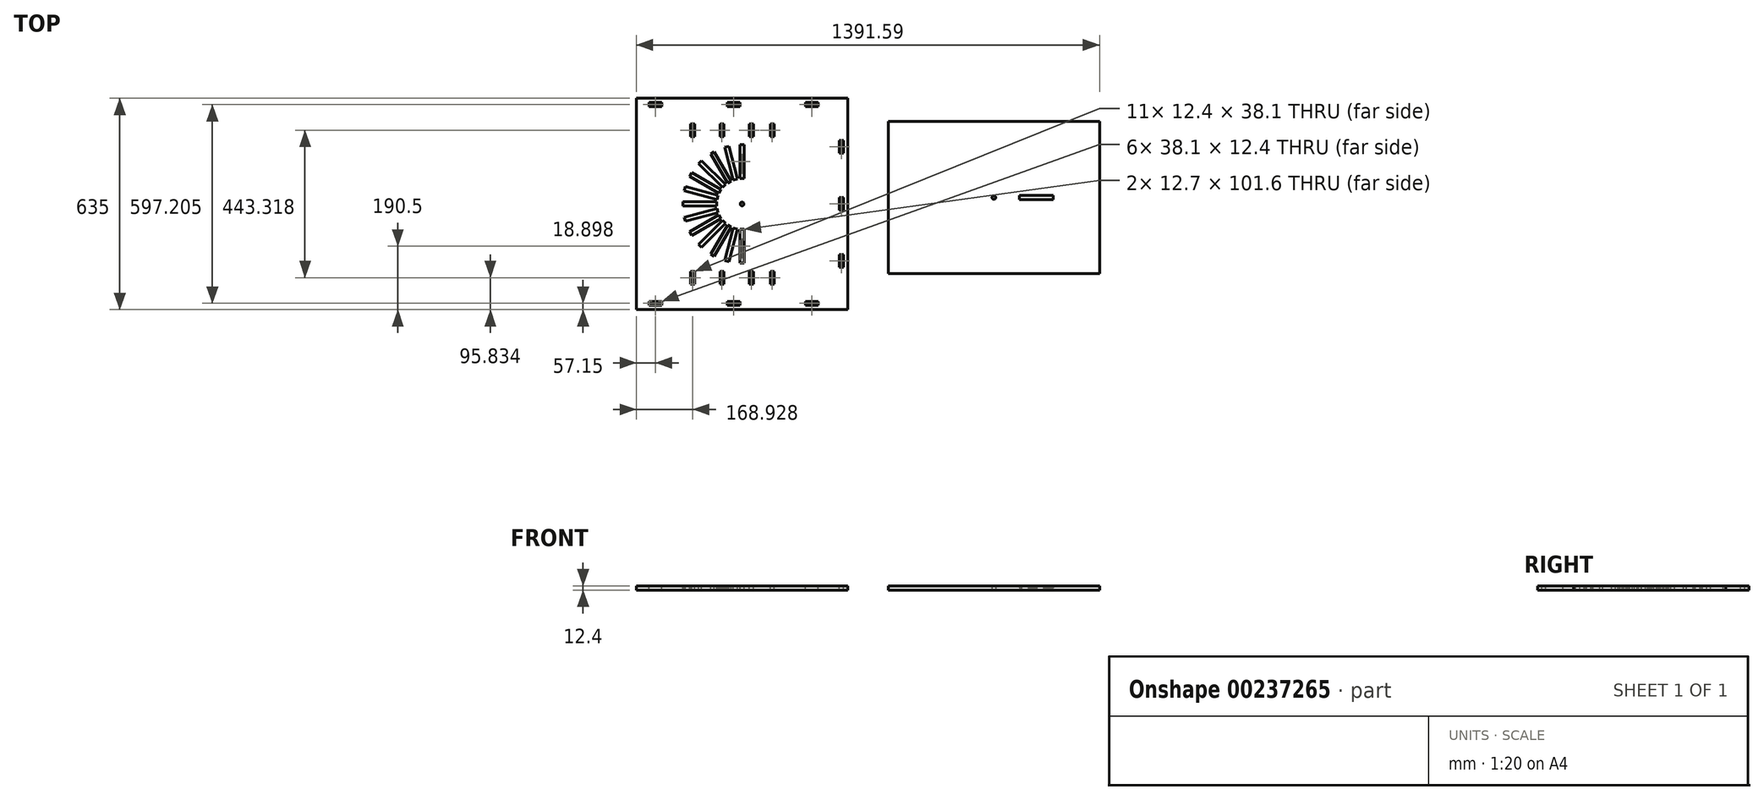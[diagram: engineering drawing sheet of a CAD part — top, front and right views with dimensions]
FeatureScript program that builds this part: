
annotation { "Feature Type Name" : "Feature", "Feature Type Description" : "" }
export const myFeature = defineFeature(function(context is Context, id is Id, definition is map)
    precondition{}
    {
        {
            var Q0;
            Q0=qCreatedBy(makeId("Top.planeOp"),FACE);
            var sketch = newSketch(context, id + "F0", { "sketchPlane" : qUnion([Q0])});
            skLineSegment(sketch, "E0.bottom", {"start": v(0, 0) * mm, "end": v(635, 0) * mm});
            skLineSegment(sketch, "E0.top", {"start": v(0, 635) * mm, "end": v(635, 635) * mm});
            skLineSegment(sketch, "E0.left", {"start": v(0, 0) * mm, "end": v(0, 635) * mm});
            skLineSegment(sketch, "E0.right", {"start": v(635, 0) * mm, "end": v(635, 635) * mm});
            skCircle(sketch, "E1", {"center": v(317.5, 317.5) * mm, "radius": 5.56 * mm});
            skPoint(sketch, "E1.centerSnap0", {"position": v(317.5, 0) * mm});
            skPoint(sketch, "E1.centerSnap1", {"position": v(0, 317.5) * mm});
            skLineSegment(sketch, "E2.bottom", {"start": v(756.6, 108.1) * mm, "end": v(1391.6, 108.1) * mm});
            skLineSegment(sketch, "E2.top", {"start": v(756.6, 565.3) * mm, "end": v(1391.6, 565.3) * mm});
            skLineSegment(sketch, "E2.left", {"start": v(756.6, 108.1) * mm, "end": v(756.6, 565.3) * mm});
            skLineSegment(sketch, "E2.right", {"start": v(1391.6, 108.1) * mm, "end": v(1391.6, 565.3) * mm});
            skCircle(sketch, "E3", {"center": v(1074.1, 336.7) * mm, "radius": 5.56 * mm});
            skPoint(sketch, "E3.centerSnap0", {"position": v(1074.1, 108.1) * mm});
            skPoint(sketch, "E3.centerSnap1", {"position": v(756.6, 336.7) * mm});
            skLineSegment(sketch, "E4.bottom", {"start": v(1251.9, 343.05) * mm, "end": v(1150.3, 343.05) * mm});
            skLineSegment(sketch, "E4.top", {"start": v(1251.9, 330.35) * mm, "end": v(1150.3, 330.35) * mm});
            skLineSegment(sketch, "E4.left", {"start": v(1251.9, 343.05) * mm, "end": v(1251.9, 330.35) * mm});
            skLineSegment(sketch, "E4.right", {"start": v(1150.3, 343.05) * mm, "end": v(1150.3, 330.35) * mm});
            skPoint(sketch, "E4.middle", {"position": v(1201.1, 336.7) * mm});
            skPoint(sketch, "E4.middle.positionSnap0", {"position": v(1391.6, 336.7) * mm});
            skPoint(sketch, "E4.centerSnap0", {"position": v(1391.6, 336.7) * mm});
            skSolve(sketch);
        }
        {
            var Q0;
            Q0 = qSketchRegion(id + "F0", true);
            extrude(context, id + "F1", {"entities" : qUnion([Q0]), "depth" : 12.4 * mm});
        }
        {
            var Q0;
            Q0=makeQuery(id+"F1.opExtrude","CAP_FACE",FACE,{"disambiguationData":[OSD([sQuery(id+"F0.wireOp",EDGE,"E0.bottom"),sQuery(id+"F0.wireOp",EDGE,"E0.top"),sQuery(id+"F0.wireOp",EDGE,"E0.left"),sQuery(id+"F0.wireOp",EDGE,"E0.right"),sQuery(id+"F0.wireOp",EDGE,"E1")])],"isStart":false});
            var sketch = newSketch(context, id + "F2", { "sketchPlane" : qUnion([Q0])});
            skLineSegment(sketch, "E5.bottom", {"start": v(38.1, 622.3) * mm, "end": v(76.2, 622.3) * mm});
            skLineSegment(sketch, "E5.top", {"start": v(38.1, 609.9) * mm, "end": v(76.2, 609.9) * mm});
            skLineSegment(sketch, "E5.left", {"start": v(38.1, 622.3) * mm, "end": v(38.1, 609.9) * mm});
            skLineSegment(sketch, "E5.right", {"start": v(76.2, 622.3) * mm, "end": v(76.2, 609.9) * mm});
            skLineSegment(sketch, "E6.bottom", {"start": v(273.05, 622.3) * mm, "end": v(311.15, 622.3) * mm});
            skLineSegment(sketch, "E6.top", {"start": v(273.05, 609.9) * mm, "end": v(311.15, 609.9) * mm});
            skLineSegment(sketch, "E6.left", {"start": v(273.05, 622.3) * mm, "end": v(273.05, 609.9) * mm});
            skLineSegment(sketch, "E6.right", {"start": v(311.15, 622.3) * mm, "end": v(311.15, 609.9) * mm});
            skLineSegment(sketch, "E7.bottom", {"start": v(508, 622.3) * mm, "end": v(546.1, 622.3) * mm});
            skLineSegment(sketch, "E7.top", {"start": v(508, 609.9) * mm, "end": v(546.1, 609.9) * mm});
            skLineSegment(sketch, "E7.left", {"start": v(508, 622.3) * mm, "end": v(508, 609.9) * mm});
            skLineSegment(sketch, "E7.right", {"start": v(546.1, 622.3) * mm, "end": v(546.1, 609.9) * mm});
            skLineSegment(sketch, "E8", {"start": v(0, 317.5) * mm, "end": v(635, 317.5) * mm});
            skLineSegment(sketch, "E9.bottom", {"start": v(76.2, 12.7) * mm, "end": v(38.1, 12.7) * mm});
            skLineSegment(sketch, "E9.top", {"start": v(76.2, 25.1) * mm, "end": v(38.1, 25.1) * mm});
            skLineSegment(sketch, "E9.left", {"start": v(76.2, 12.7) * mm, "end": v(76.2, 25.1) * mm});
            skLineSegment(sketch, "E9.right", {"start": v(38.1, 12.7) * mm, "end": v(38.1, 25.1) * mm});
            skLineSegment(sketch, "E10.bottom", {"start": v(273.05, 25.1) * mm, "end": v(311.15, 25.1) * mm});
            skLineSegment(sketch, "E10.top", {"start": v(273.05, 12.7) * mm, "end": v(311.15, 12.7) * mm});
            skLineSegment(sketch, "E10.left", {"start": v(273.05, 25.1) * mm, "end": v(273.05, 12.7) * mm});
            skLineSegment(sketch, "E10.right", {"start": v(311.15, 25.1) * mm, "end": v(311.15, 12.7) * mm});
            skLineSegment(sketch, "E11.bottom", {"start": v(508, 25.1) * mm, "end": v(546.1, 25.1) * mm});
            skLineSegment(sketch, "E11.top", {"start": v(508, 12.7) * mm, "end": v(546.1, 12.7) * mm});
            skLineSegment(sketch, "E11.left", {"start": v(508, 25.1) * mm, "end": v(508, 12.7) * mm});
            skLineSegment(sketch, "E11.right", {"start": v(546.1, 25.1) * mm, "end": v(546.1, 12.7) * mm});
            skLineSegment(sketch, "E12.bottom", {"start": v(609.9, 336.55) * mm, "end": v(622.3, 336.55) * mm});
            skLineSegment(sketch, "E12.top", {"start": v(609.9, 298.45) * mm, "end": v(622.3, 298.45) * mm});
            skLineSegment(sketch, "E12.left", {"start": v(609.9, 336.55) * mm, "end": v(609.9, 298.45) * mm});
            skLineSegment(sketch, "E12.right", {"start": v(622.3, 336.55) * mm, "end": v(622.3, 298.45) * mm});
            skPoint(sketch, "E12.middle", {"position": v(616.1, 317.5) * mm});
            skLineSegment(sketch, "E13.bottom", {"start": v(622.3, 469.9) * mm, "end": v(609.9, 469.9) * mm});
            skLineSegment(sketch, "E13.top", {"start": v(622.3, 508) * mm, "end": v(609.9, 508) * mm});
            skLineSegment(sketch, "E13.left", {"start": v(622.3, 469.9) * mm, "end": v(622.3, 508) * mm});
            skLineSegment(sketch, "E13.right", {"start": v(609.9, 469.9) * mm, "end": v(609.9, 508) * mm});
            skPoint(sketch, "E13.middle", {"position": v(616.1, 488.95) * mm});
            skLineSegment(sketch, "E14.bottom", {"start": v(622.3, 127) * mm, "end": v(609.9, 127) * mm});
            skLineSegment(sketch, "E14.top", {"start": v(622.3, 165.1) * mm, "end": v(609.9, 165.1) * mm});
            skLineSegment(sketch, "E14.left", {"start": v(622.3, 127) * mm, "end": v(622.3, 165.1) * mm});
            skLineSegment(sketch, "E14.right", {"start": v(609.9, 127) * mm, "end": v(609.9, 165.1) * mm});
            skPoint(sketch, "E14.middle", {"position": v(616.1, 146.05) * mm});
            skLineSegment(sketch, "E15.bottom", {"start": v(402.2, 114.9) * mm, "end": v(414.6, 114.9) * mm});
            skLineSegment(sketch, "E15.top", {"start": v(402.2, 76.8) * mm, "end": v(414.6, 76.8) * mm});
            skLineSegment(sketch, "E15.left", {"start": v(402.2, 114.9) * mm, "end": v(402.2, 76.8) * mm});
            skLineSegment(sketch, "E15.right", {"start": v(414.6, 114.9) * mm, "end": v(414.6, 76.8) * mm});
            skLineSegment(sketch, "E16.bottom", {"start": v(339.31, 114.88) * mm, "end": v(351.7, 114.88) * mm});
            skLineSegment(sketch, "E16.top", {"start": v(339.31, 76.78) * mm, "end": v(351.7, 76.78) * mm});
            skLineSegment(sketch, "E16.left", {"start": v(339.31, 114.88) * mm, "end": v(339.31, 76.78) * mm});
            skLineSegment(sketch, "E16.right", {"start": v(351.7, 114.88) * mm, "end": v(351.7, 76.78) * mm});
            skLineSegment(sketch, "E17.bottom", {"start": v(251.02, 114.88) * mm, "end": v(263.42, 114.88) * mm});
            skLineSegment(sketch, "E17.top", {"start": v(251.02, 76.78) * mm, "end": v(263.42, 76.78) * mm});
            skLineSegment(sketch, "E17.left", {"start": v(251.02, 114.88) * mm, "end": v(251.02, 76.78) * mm});
            skLineSegment(sketch, "E17.right", {"start": v(263.42, 114.88) * mm, "end": v(263.42, 76.78) * mm});
            skLineSegment(sketch, "E18.bottom", {"start": v(162.73, 114.88) * mm, "end": v(175.13, 114.88) * mm});
            skLineSegment(sketch, "E18.top", {"start": v(162.73, 76.78) * mm, "end": v(175.13, 76.78) * mm});
            skLineSegment(sketch, "E18.left", {"start": v(162.73, 114.88) * mm, "end": v(162.73, 76.78) * mm});
            skLineSegment(sketch, "E18.right", {"start": v(175.13, 114.88) * mm, "end": v(175.13, 76.78) * mm});
            skLineSegment(sketch, "E19.bottom", {"start": v(414.6, 558.2) * mm, "end": v(402.2, 558.2) * mm});
            skLineSegment(sketch, "E19.top", {"start": v(414.6, 520.1) * mm, "end": v(402.2, 520.1) * mm});
            skLineSegment(sketch, "E19.left", {"start": v(414.6, 558.2) * mm, "end": v(414.6, 520.1) * mm});
            skLineSegment(sketch, "E19.right", {"start": v(402.2, 558.2) * mm, "end": v(402.2, 520.1) * mm});
            skLineSegment(sketch, "E20.bottom", {"start": v(351.7, 520.1) * mm, "end": v(339.31, 520.1) * mm});
            skLineSegment(sketch, "E20.top", {"start": v(351.7, 558.2) * mm, "end": v(339.31, 558.2) * mm});
            skLineSegment(sketch, "E20.left", {"start": v(351.7, 520.1) * mm, "end": v(351.7, 558.2) * mm});
            skLineSegment(sketch, "E20.right", {"start": v(339.31, 520.1) * mm, "end": v(339.31, 558.2) * mm});
            skLineSegment(sketch, "E21.bottom", {"start": v(263.42, 520.1) * mm, "end": v(251.02, 520.1) * mm});
            skLineSegment(sketch, "E21.top", {"start": v(263.42, 558.2) * mm, "end": v(251.02, 558.2) * mm});
            skLineSegment(sketch, "E21.left", {"start": v(263.42, 520.1) * mm, "end": v(263.42, 558.2) * mm});
            skLineSegment(sketch, "E21.right", {"start": v(251.02, 520.1) * mm, "end": v(251.02, 558.2) * mm});
            skLineSegment(sketch, "E22.bottom", {"start": v(175.13, 520.1) * mm, "end": v(162.73, 520.1) * mm});
            skLineSegment(sketch, "E22.top", {"start": v(175.13, 558.2) * mm, "end": v(162.73, 558.2) * mm});
            skLineSegment(sketch, "E22.left", {"start": v(175.13, 520.1) * mm, "end": v(175.13, 558.2) * mm});
            skLineSegment(sketch, "E22.right", {"start": v(162.73, 520.1) * mm, "end": v(162.73, 558.2) * mm});
            skSolve(sketch);
        }
        {
            var Q0;
            Q0=makeQuery(id+"F2.imprint","IMPRINT",FACE,{"disambiguationData":[TD([[makeQuery(id+"F2.imprint","IMPRINT",EDGE,{"derivedFrom":sQuery(id+"F2.wireOp",EDGE,"E5.bottom")}),-1.0]])]});
            var Q1;
            Q1=makeQuery(id+"F2.imprint","IMPRINT",FACE,{"disambiguationData":[TD([[makeQuery(id+"F2.imprint","IMPRINT",EDGE,{"derivedFrom":sQuery(id+"F2.wireOp",EDGE,"E6.bottom")}),-1.0]])]});
            var Q2;
            Q2=makeQuery(id+"F2.imprint","IMPRINT",FACE,{"disambiguationData":[TD([[makeQuery(id+"F2.imprint","IMPRINT",EDGE,{"derivedFrom":sQuery(id+"F2.wireOp",EDGE,"E7.bottom")}),-1.0]])]});
            var Q3;
            Q3=makeQuery(id+"F2.imprint","IMPRINT",FACE,{"disambiguationData":[TD([[makeQuery(id+"F2.imprint","IMPRINT",EDGE,{"derivedFrom":sQuery(id+"F2.wireOp",EDGE,"E9.bottom")}),-1.0]])]});
            var Q4;
            Q4=makeQuery(id+"F2.imprint","IMPRINT",FACE,{"disambiguationData":[TD([[makeQuery(id+"F2.imprint","IMPRINT",EDGE,{"derivedFrom":sQuery(id+"F2.wireOp",EDGE,"E10.bottom")}),-1.0]])]});
            var Q5;
            Q5=makeQuery(id+"F2.imprint","IMPRINT",FACE,{"disambiguationData":[TD([[makeQuery(id+"F2.imprint","IMPRINT",EDGE,{"derivedFrom":sQuery(id+"F2.wireOp",EDGE,"E11.bottom")}),-1.0]])]});
            var Q6;
            Q6=makeQuery(id+"F2.imprint","IMPRINT",FACE,{"disambiguationData":[TD([[makeQuery(id+"F2.imprint","IMPRINT",EDGE,{"derivedFrom":sQuery(id+"F2.wireOp",EDGE,"E13.bottom")}),-1.0]])]});
            var Q7;
            Q7=makeQuery(id+"F2.imprint","IMPRINT",FACE,{"disambiguationData":[TD([[makeQuery(id+"F2.imprint","IMPRINT",EDGE,{"derivedFrom":sQuery(id+"F2.wireOp",EDGE,"E12.bottom")}),-1.0]])]});
            var Q8;
            Q8=makeQuery(id+"F2.imprint","IMPRINT",FACE,{"disambiguationData":[TD([[makeQuery(id+"F2.imprint","IMPRINT",EDGE,{"derivedFrom":sQuery(id+"F2.wireOp",EDGE,"E14.bottom")}),-1.0]])]});
            var Q9;
            Q9=makeQuery(id+"F2.imprint","IMPRINT",FACE,{"disambiguationData":[TD([[makeQuery(id+"F2.imprint","IMPRINT",EDGE,{"derivedFrom":sQuery(id+"F2.wireOp",EDGE,"SUhSXul5-Doog-AFDD-ChaY-rLmTJKXzFGPb.bottom")}),-1.0]])]});
            var Q10;
            Q10=makeQuery(id+"F2.imprint","IMPRINT",FACE,{"disambiguationData":[TD([[makeQuery(id+"F2.imprint","IMPRINT",EDGE,{"derivedFrom":sQuery(id+"F2.wireOp",EDGE,"8pVk5TjY-WfAx-fIYx-P9lx-uP9n1sAqBUMo.bottom")}),-1.0]])]});
            var Q11;
            Q11=makeQuery(id+"F2.imprint","IMPRINT",FACE,{"disambiguationData":[TD([[makeQuery(id+"F2.imprint","IMPRINT",EDGE,{"derivedFrom":sQuery(id+"F2.wireOp",EDGE,"E15.bottom")}),-1.0]])]});
            var Q12;
            Q12=makeQuery(id+"F2.imprint","IMPRINT",FACE,{"disambiguationData":[TD([[makeQuery(id+"F2.imprint","IMPRINT",EDGE,{"derivedFrom":sQuery(id+"F2.wireOp",EDGE,"E16.bottom")}),-1.0]])]});
            var Q13;
            Q13=makeQuery(id+"F2.imprint","IMPRINT",FACE,{"disambiguationData":[TD([[makeQuery(id+"F2.imprint","IMPRINT",EDGE,{"derivedFrom":sQuery(id+"F2.wireOp",EDGE,"E18.bottom")}),-1.0]])]});
            var Q14;
            Q14=makeQuery(id+"F2.imprint","IMPRINT",FACE,{"disambiguationData":[TD([[makeQuery(id+"F2.imprint","IMPRINT",EDGE,{"derivedFrom":sQuery(id+"F2.wireOp",EDGE,"E17.bottom")}),-1.0]])]});
            var Q15;
            Q15=makeQuery(id+"F2.imprint","IMPRINT",FACE,{"disambiguationData":[TD([[makeQuery(id+"F2.imprint","IMPRINT",EDGE,{"derivedFrom":sQuery(id+"F2.wireOp",EDGE,"E22.bottom")}),-1.0]])]});
            var Q16;
            Q16=makeQuery(id+"F2.imprint","IMPRINT",FACE,{"disambiguationData":[TD([[makeQuery(id+"F2.imprint","IMPRINT",EDGE,{"derivedFrom":sQuery(id+"F2.wireOp",EDGE,"E21.bottom")}),-1.0]])]});
            var Q17;
            Q17=makeQuery(id+"F2.imprint","IMPRINT",FACE,{"disambiguationData":[TD([[makeQuery(id+"F2.imprint","IMPRINT",EDGE,{"derivedFrom":sQuery(id+"F2.wireOp",EDGE,"E20.bottom")}),-1.0]])]});
            var Q18;
            Q18=makeQuery(id+"F2.imprint","IMPRINT",FACE,{"disambiguationData":[TD([[makeQuery(id+"F2.imprint","IMPRINT",EDGE,{"derivedFrom":sQuery(id+"F2.wireOp",EDGE,"E19.bottom")}),1.0]])]});
            var Q19;
            {var subQ5=sQuery(id+"F2.wireOp",EDGE,"E12.top");Q19=makeQuery(id+"F2.imprint","IMPRINT",FACE,{"disambiguationData":[TD([[makeQuery(id+"F2.imprint","IMPRINT",EDGE,{"derivedFrom":subQ5}),1.0]])]});}
            extrude(context, id + "F3", {"entities" : qUnion([Q0, Q1, Q2, Q3, Q4, Q5, Q6, Q7, Q8, Q9, Q10, Q11, Q12, Q13, Q14, Q15, Q16, Q17, Q18, Q19]), "operationType" : NewBodyOperationType.REMOVE, "oppositeDirection" : true, "depth" : 12.4 * mm});
        }
        {
            var Q0;
            Q0=makeQuery(id+"F0.imprint","IMPRINT",FACE,{"disambiguationData":[TD([[makeQuery(id+"F0.imprint","IMPRINT",EDGE,{"derivedFrom":sQuery(id+"F0.wireOp",EDGE,"E4.bottom")}),1.0]])]});
            extrude(context, id + "F4", {"entities" : qUnion([Q0]), "operationType" : NewBodyOperationType.ADD, "depth" : 6.35 * mm});
        }
        {
            var Q0;
            Q0=makeQuery(id+"F1.opExtrude","CAP_FACE",FACE,{"disambiguationData":[OSD([sQuery(id+"F0.wireOp",EDGE,"E0.bottom"),sQuery(id+"F0.wireOp",EDGE,"E0.top"),sQuery(id+"F0.wireOp",EDGE,"E0.left"),sQuery(id+"F0.wireOp",EDGE,"E0.right"),sQuery(id+"F0.wireOp",EDGE,"E1")])],"isStart":false});
            var sketch = newSketch(context, id + "F5", { "sketchPlane" : qUnion([Q0])});
            skLineSegment(sketch, "E23", {"start": v(317.5, 317.5) * mm, "end": v(317.5, 491.42) * mm, "construction": true});
            skLineSegment(sketch, "E24.bottom", {"start": v(323.85, 393.7) * mm, "end": v(311.15, 393.7) * mm});
            skLineSegment(sketch, "E24.top", {"start": v(323.85, 495.3) * mm, "end": v(311.15, 495.3) * mm});
            skLineSegment(sketch, "E24.left", {"start": v(323.85, 393.7) * mm, "end": v(323.85, 495.3) * mm});
            skLineSegment(sketch, "E24.right", {"start": v(311.15, 393.7) * mm, "end": v(311.15, 495.3) * mm});
            skPoint(sketch, "E24.middle", {"position": v(317.5, 444.5) * mm});
            skLineSegment(sketch, "E25.1.0", {"start": v(277.62, 490.89) * mm, "end": v(265.35, 487.6) * mm});
            skLineSegment(sketch, "E25.1.1", {"start": v(303.91, 392.75) * mm, "end": v(277.62, 490.89) * mm});
            skLineSegment(sketch, "E25.1.2", {"start": v(291.64, 389.46) * mm, "end": v(265.35, 487.6) * mm});
            skLineSegment(sketch, "E25.1.3", {"start": v(303.91, 392.75) * mm, "end": v(291.64, 389.46) * mm});
            skLineSegment(sketch, "E25.2.0", {"start": v(234.1, 474.65) * mm, "end": v(223.1, 468.3) * mm});
            skLineSegment(sketch, "E25.2.1", {"start": v(284.9, 386.67) * mm, "end": v(234.1, 474.65) * mm});
            skLineSegment(sketch, "E25.2.2", {"start": v(273.9, 380.32) * mm, "end": v(223.1, 468.3) * mm});
            skLineSegment(sketch, "E25.2.3", {"start": v(284.9, 386.67) * mm, "end": v(273.9, 380.32) * mm});
            skPoint(sketch, "E25.center", {"position": v(317.5, 317.5) * mm});
            skLineSegment(sketch, "E26.3.3.0", {"start": v(268.1, 375.87) * mm, "end": v(196.27, 447.71) * mm});
            skLineSegment(sketch, "E26.6.3.0", {"start": v(259.13, 366.9) * mm, "end": v(187.29, 438.73) * mm});
            skLineSegment(sketch, "E26.7.3.0", {"start": v(196.27, 447.71) * mm, "end": v(187.29, 438.73) * mm});
            skLineSegment(sketch, "E26.9.3.0", {"start": v(268.1, 375.87) * mm, "end": v(259.13, 366.9) * mm});
            skLineSegment(sketch, "E26.3.4.0", {"start": v(254.68, 361.1) * mm, "end": v(166.7, 411.9) * mm});
            skLineSegment(sketch, "E26.6.4.0", {"start": v(248.33, 350.1) * mm, "end": v(160.35, 400.9) * mm});
            skLineSegment(sketch, "E26.7.4.0", {"start": v(166.7, 411.9) * mm, "end": v(160.35, 400.9) * mm});
            skLineSegment(sketch, "E26.9.4.0", {"start": v(254.68, 361.1) * mm, "end": v(248.33, 350.1) * mm});
            skLineSegment(sketch, "E26.3.5.0", {"start": v(245.54, 343.36) * mm, "end": v(147.4, 369.65) * mm});
            skLineSegment(sketch, "E26.6.5.0", {"start": v(242.25, 331.09) * mm, "end": v(144.11, 357.38) * mm});
            skLineSegment(sketch, "E26.7.5.0", {"start": v(147.4, 369.65) * mm, "end": v(144.11, 357.38) * mm});
            skLineSegment(sketch, "E26.9.5.0", {"start": v(245.54, 343.36) * mm, "end": v(242.25, 331.09) * mm});
            skLineSegment(sketch, "E26.3.6.0", {"start": v(241.3, 323.85) * mm, "end": v(139.7, 323.85) * mm});
            skLineSegment(sketch, "E26.6.6.0", {"start": v(241.3, 311.15) * mm, "end": v(139.7, 311.15) * mm});
            skLineSegment(sketch, "E26.7.6.0", {"start": v(139.7, 323.85) * mm, "end": v(139.7, 311.15) * mm});
            skLineSegment(sketch, "E26.9.6.0", {"start": v(241.3, 323.85) * mm, "end": v(241.3, 311.15) * mm});
            skLineSegment(sketch, "E26.3.7.0", {"start": v(242.25, 303.91) * mm, "end": v(144.11, 277.62) * mm});
            skLineSegment(sketch, "E26.6.7.0", {"start": v(245.54, 291.64) * mm, "end": v(147.4, 265.35) * mm});
            skLineSegment(sketch, "E26.7.7.0", {"start": v(144.11, 277.62) * mm, "end": v(147.4, 265.35) * mm});
            skLineSegment(sketch, "E26.9.7.0", {"start": v(242.25, 303.91) * mm, "end": v(245.54, 291.64) * mm});
            skLineSegment(sketch, "E26.3.8.0", {"start": v(248.33, 284.9) * mm, "end": v(160.35, 234.1) * mm});
            skLineSegment(sketch, "E26.6.8.0", {"start": v(254.68, 273.9) * mm, "end": v(166.7, 223.1) * mm});
            skLineSegment(sketch, "E26.7.8.0", {"start": v(160.35, 234.1) * mm, "end": v(166.7, 223.1) * mm});
            skLineSegment(sketch, "E26.9.8.0", {"start": v(248.33, 284.9) * mm, "end": v(254.68, 273.9) * mm});
            skLineSegment(sketch, "E26.3.9.0", {"start": v(259.13, 268.1) * mm, "end": v(187.29, 196.27) * mm});
            skLineSegment(sketch, "E26.6.9.0", {"start": v(268.1, 259.13) * mm, "end": v(196.27, 187.29) * mm});
            skLineSegment(sketch, "E26.7.9.0", {"start": v(187.29, 196.27) * mm, "end": v(196.27, 187.29) * mm});
            skLineSegment(sketch, "E26.9.9.0", {"start": v(259.13, 268.1) * mm, "end": v(268.1, 259.13) * mm});
            skLineSegment(sketch, "E26.3.10.0", {"start": v(273.9, 254.68) * mm, "end": v(223.1, 166.7) * mm});
            skLineSegment(sketch, "E26.6.10.0", {"start": v(284.9, 248.33) * mm, "end": v(234.1, 160.35) * mm});
            skLineSegment(sketch, "E26.7.10.0", {"start": v(223.1, 166.7) * mm, "end": v(234.1, 160.35) * mm});
            skLineSegment(sketch, "E26.9.10.0", {"start": v(273.9, 254.68) * mm, "end": v(284.9, 248.33) * mm});
            skLineSegment(sketch, "E26.3.11.0", {"start": v(291.64, 245.54) * mm, "end": v(265.35, 147.4) * mm});
            skLineSegment(sketch, "E26.6.11.0", {"start": v(303.91, 242.25) * mm, "end": v(277.62, 144.11) * mm});
            skLineSegment(sketch, "E26.7.11.0", {"start": v(265.35, 147.4) * mm, "end": v(277.62, 144.11) * mm});
            skLineSegment(sketch, "E26.9.11.0", {"start": v(291.64, 245.54) * mm, "end": v(303.91, 242.25) * mm});
            skLineSegment(sketch, "E26.3.12.0", {"start": v(311.15, 241.3) * mm, "end": v(311.15, 139.7) * mm});
            skLineSegment(sketch, "E26.6.12.0", {"start": v(323.85, 241.3) * mm, "end": v(323.85, 139.7) * mm});
            skLineSegment(sketch, "E26.7.12.0", {"start": v(311.15, 139.7) * mm, "end": v(323.85, 139.7) * mm});
            skLineSegment(sketch, "E26.9.12.0", {"start": v(311.15, 241.3) * mm, "end": v(323.85, 241.3) * mm});
            skSolve(sketch);
        }
        {
            var Q0;
            Q0 = qSketchRegion(id + "F5", true);
            extrude(context, id + "F6", {"entities" : qUnion([Q0]), "operationType" : NewBodyOperationType.REMOVE, "endBound" : BoundingType.UP_TO_NEXT, "oppositeDirection" : true, "depth" : 25.4 * mm});
        }
    });
